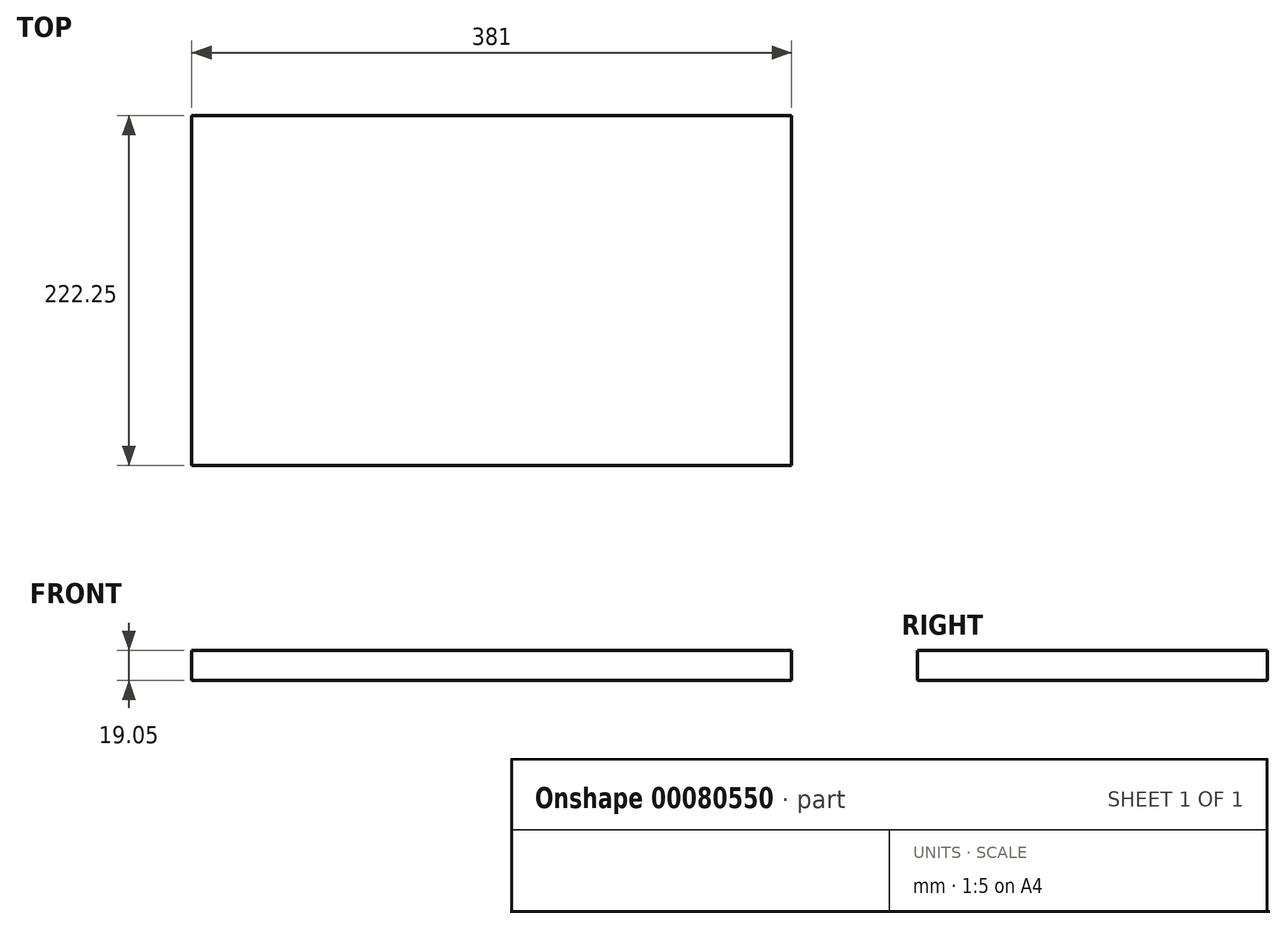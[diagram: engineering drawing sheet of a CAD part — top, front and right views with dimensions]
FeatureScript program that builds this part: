
annotation { "Feature Type Name" : "Feature", "Feature Type Description" : "" }
export const myFeature = defineFeature(function(context is Context, id is Id, definition is map)
    precondition{}
    {
        {
            var Q0;
            Q0=qCreatedBy(makeId("Top.planeOp"),FACE);
            var sketch = newSketch(context, id + "F0", { "sketchPlane" : qUnion([Q0])});
            skLineSegment(sketch, "E0.bottom", {"start": v(0, 0) * mm, "end": v(-381, 0) * mm});
            skLineSegment(sketch, "E0.top", {"start": v(0, -222.25) * mm, "end": v(-381, -222.25) * mm});
            skLineSegment(sketch, "E0.left", {"start": v(0, 0) * mm, "end": v(0, -222.25) * mm});
            skLineSegment(sketch, "E0.right", {"start": v(-381, 0) * mm, "end": v(-381, -222.25) * mm});
            skSolve(sketch);
        }
        {
            var Q0;
            Q0=makeQuery(id+"F0.imprint","IMPRINT",FACE,{"disambiguationData":[TD([[makeQuery(id+"F0.imprint","IMPRINT",EDGE,{"derivedFrom":sQuery(id+"F0.wireOp",EDGE,"E0.bottom")}),1.0]])]});
            extrude(context, id + "F1", {"entities" : qUnion([Q0]), "depth" : 19.05 * mm});
        }
    });
